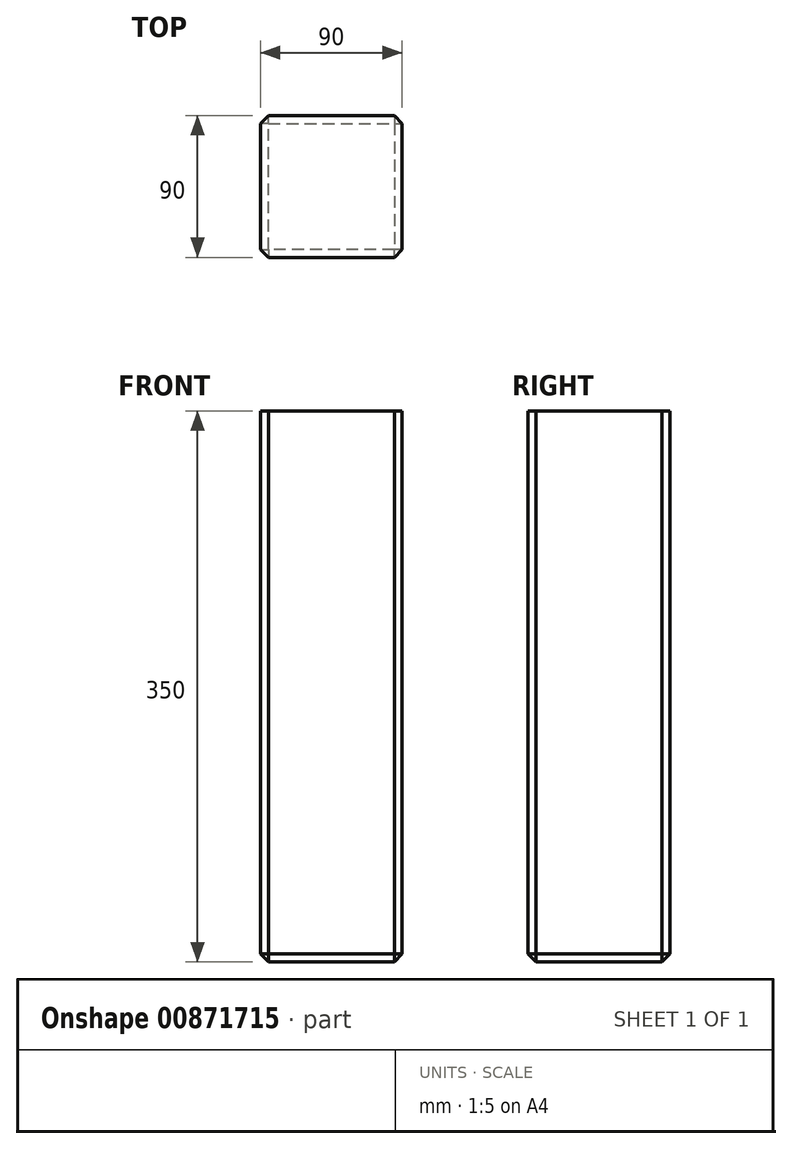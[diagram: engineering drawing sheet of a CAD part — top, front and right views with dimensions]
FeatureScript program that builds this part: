
annotation { "Feature Type Name" : "Feature", "Feature Type Description" : "" }
export const myFeature = defineFeature(function(context is Context, id is Id, definition is map)
    precondition{}
    {
        {
            var Q0;
            Q0=qCreatedBy(makeId("Front.planeOp"),FACE);
            var sketch = newSketch(context, id + "F0", { "sketchPlane" : qUnion([Q0])});
            skLineSegment(sketch, "E0.bottom", {"start": v(0, 0) * mm, "end": v(90, 0) * mm});
            skLineSegment(sketch, "E0.top", {"start": v(0, 300) * mm, "end": v(90, 300) * mm});
            skLineSegment(sketch, "E0.left", {"start": v(0, 0) * mm, "end": v(0, 300) * mm});
            skLineSegment(sketch, "E0.right", {"start": v(90, 0) * mm, "end": v(90, 300) * mm});
            skSolve(sketch);
        }
        {
            var Q0;
            Q0 = qSketchRegion(id + "F0", true);
            extrude(context, id + "F1", {"entities" : qUnion([Q0]), "depth" : 90 * mm, "offsetDistance" : 25 * mm});
        }
        {
            var Q0;
            Q0=makeQuery(id+"F1.opExtrude","CAP_EDGE",EDGE,{"disambiguationData":[OSD([sQuery(id+"F0.wireOp",EDGE,"E0.right")])],"isStart":false});
            var Q1;
            Q1=makeQuery(id+"F1.opExtrude","CAP_EDGE",EDGE,{"disambiguationData":[OSD([sQuery(id+"F0.wireOp",EDGE,"E0.left")])],"isStart":false});
            var Q2;
            Q2=makeQuery(id+"F1.opExtrude","CAP_EDGE",EDGE,{"disambiguationData":[OSD([sQuery(id+"F0.wireOp",EDGE,"E0.right")])],"isStart":true});
            var Q3;
            Q3=makeQuery(id+"F1.opExtrude","CAP_EDGE",EDGE,{"disambiguationData":[OSD([sQuery(id+"F0.wireOp",EDGE,"E0.left")])],"isStart":true});
            var Q4;
            Q4=makeQuery(id+"F1.opExtrude","CAP_EDGE",EDGE,{"disambiguationData":[OSD([sQuery(id+"F0.wireOp",EDGE,"E0.bottom")])],"isStart":true});
            var Q5;
            Q5=makeQuery(id+"F1.opExtrude","SWEPT_EDGE",EDGE,{"disambiguationData":[OSD([sQuery(id+"F0.wireOp",EDGE,"E0.bottom"),sQuery(id+"F0.wireOp",EDGE,"E0.left")])]});
            var Q6;
            Q6=makeQuery(id+"F1.opExtrude","CAP_EDGE",EDGE,{"disambiguationData":[OSD([sQuery(id+"F0.wireOp",EDGE,"E0.bottom")])],"isStart":false});
            var Q7;
            Q7=makeQuery(id+"F1.opExtrude","SWEPT_EDGE",EDGE,{"disambiguationData":[OSD([sQuery(id+"F0.wireOp",EDGE,"E0.bottom"),sQuery(id+"F0.wireOp",EDGE,"E0.right")])]});
            chamfer(context, id + "F2", {"entities" : qUnion([Q0, Q1, Q2, Q3, Q4, Q5, Q6, Q7]), "width" : 5 * mm, "tangentPropagation" : true});
        }
        {
            var Q0;
            Q0=makeQuery(id+"F1.opExtrude","SWEPT_FACE",FACE,{"disambiguationData":[OSD([sQuery(id+"F0.wireOp",EDGE,"E0.top")])]});
            extrude(context, id + "F3", {"entities" : qUnion([Q0]), "operationType" : NewBodyOperationType.ADD, "depth" : 50 * mm, "offsetDistance" : 25 * mm});
        }
    });
